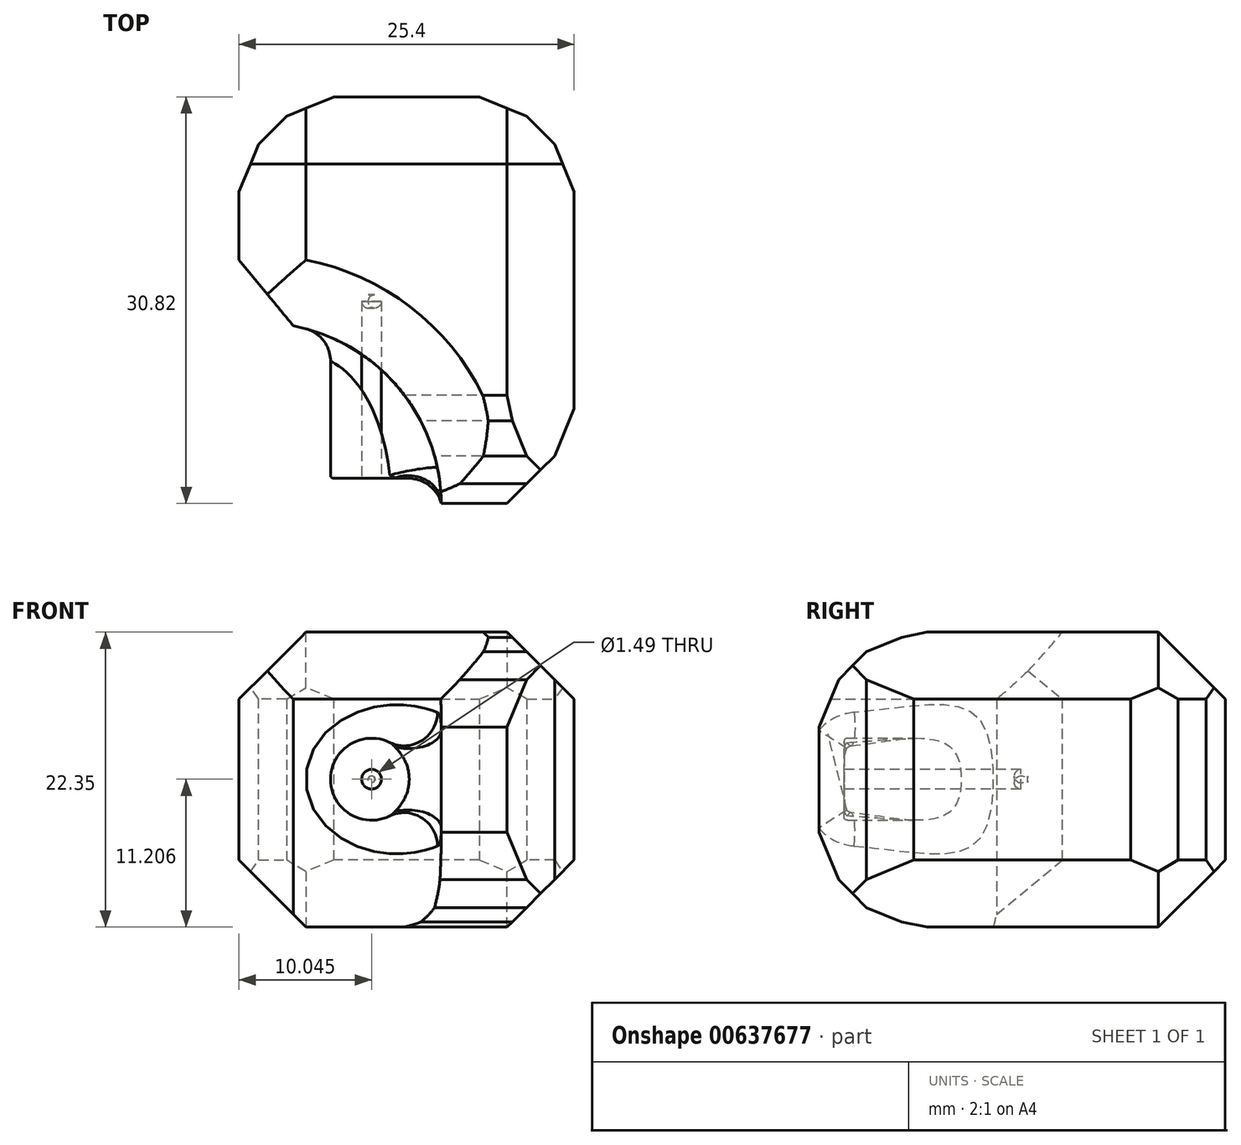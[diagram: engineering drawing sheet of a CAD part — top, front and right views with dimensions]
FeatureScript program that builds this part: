
annotation { "Feature Type Name" : "Feature", "Feature Type Description" : "" }
export const myFeature = defineFeature(function(context is Context, id is Id, definition is map)
    precondition{}
    {
        {
            var Q0;
            Q0=qCreatedBy(makeId("Top.planeOp"),FACE);
            var sketch = newSketch(context, id + "F0", { "sketchPlane" : qUnion([Q0])});
            skLineSegment(sketch, "E0.bottom", {"start": v(-10.5, 17.8) * mm, "end": v(14.9, 17.8) * mm});
            skLineSegment(sketch, "E0.top", {"start": v(-10.5, -13.03) * mm, "end": v(14.9, -13.03) * mm});
            skLineSegment(sketch, "E0.left", {"start": v(-10.5, 17.8) * mm, "end": v(-10.5, -13.03) * mm});
            skLineSegment(sketch, "E0.right", {"start": v(14.9, 17.8) * mm, "end": v(14.9, -13.03) * mm});
            skSolve(sketch);
        }
        {
            var Q0;
            Q0 = qSketchRegion(id + "F0", true);
            extrude(context, id + "F1", {"entities" : qUnion([Q0]), "depth" : 22.35 * mm, "offsetDistance" : 25.4 * mm});
        }
        {
            var Q0;
            Q0=makeQuery(id+"F1.opExtrude","SWEPT_EDGE",EDGE,{"disambiguationData":[OSD([sQuery(id+"F0.wireOp",EDGE,"E0.bottom"),sQuery(id+"F0.wireOp",EDGE,"E0.left")])]});
            var Q1;
            Q1=makeQuery(id+"F1.opExtrude","SWEPT_EDGE",EDGE,{"disambiguationData":[OSD([sQuery(id+"F0.wireOp",EDGE,"E0.bottom"),sQuery(id+"F0.wireOp",EDGE,"E0.right")])]});
            var Q2;
            Q2=makeQuery(id+"F1.opExtrude","SWEPT_EDGE",EDGE,{"disambiguationData":[OSD([sQuery(id+"F0.wireOp",EDGE,"E0.top"),sQuery(id+"F0.wireOp",EDGE,"E0.right")])]});
            var Q3;
            Q3=makeQuery(id+"F1.opExtrude","SWEPT_EDGE",EDGE,{"disambiguationData":[OSD([sQuery(id+"F0.wireOp",EDGE,"E0.top"),sQuery(id+"F0.wireOp",EDGE,"E0.left")])]});
            var Q4;
            Q4=makeQuery(id+"F1.opExtrude","CAP_EDGE",EDGE,{"disambiguationData":[OSD([sQuery(id+"F0.wireOp",EDGE,"E0.right")])],"isStart":false});
            var Q5;
            Q5=makeQuery(id+"F1.opExtrude","CAP_EDGE",EDGE,{"disambiguationData":[OSD([sQuery(id+"F0.wireOp",EDGE,"E0.right")])],"isStart":true});
            var Q6;
            Q6=makeQuery(id+"F1.opExtrude","CAP_EDGE",EDGE,{"disambiguationData":[OSD([sQuery(id+"F0.wireOp",EDGE,"E0.bottom")])],"isStart":false});
            var Q7;
            Q7=makeQuery(id+"F1.opExtrude","CAP_EDGE",EDGE,{"disambiguationData":[OSD([sQuery(id+"F0.wireOp",EDGE,"E0.bottom")])],"isStart":true});
            var Q8;
            Q8=makeQuery(id+"F1.opExtrude","CAP_EDGE",EDGE,{"disambiguationData":[OSD([sQuery(id+"F0.wireOp",EDGE,"E0.left")])],"isStart":true});
            var Q9;
            Q9=makeQuery(id+"F1.opExtrude","CAP_EDGE",EDGE,{"disambiguationData":[OSD([sQuery(id+"F0.wireOp",EDGE,"E0.left")])],"isStart":false});
            chamfer(context, id + "F2", {"entities" : qUnion([Q0, Q1, Q2, Q3, Q4, Q5, Q6, Q7, Q8, Q9]), "width" : 5.08 * mm, "tangentPropagation" : true});
        }
        {
            var Q0;
            Q0=qCreatedBy(makeId("Top.planeOp"),FACE);
            var sketch = newSketch(context, id + "F3", { "sketchPlane" : qUnion([Q0])});
            skCircle(sketch, "E1", {"center": v(-9.02, -13.17) * mm, "radius": 13.85 * mm});
            skSolve(sketch);
        }
        {
            var Q0;
            Q0=makeQuery(id+"F3.imprint","IMPRINT",FACE,{"disambiguationData":[TD([[makeQuery(id+"F3.imprint","IMPRINT",EDGE,{"derivedFrom":sQuery(id+"F3.wireOp",EDGE,"E1")}),1.0]])]});
            extrude(context, id + "F4", {"entities" : qUnion([Q0]), "operationType" : NewBodyOperationType.REMOVE, "depth" : 27.86 * mm, "offsetDistance" : 25.4 * mm});
        }
        {
            var Q0;
            Q0=qCreatedBy(makeId("Front.planeOp"),FACE);
            var sketch = newSketch(context, id + "F5", { "sketchPlane" : qUnion([Q0])});
            skCircle(sketch, "E2", {"center": v(-0.45, 11.2) * mm, "radius": 3.11 * mm});
            skSolve(sketch);
        }
        {
            var Q0;
            Q0 = qSketchRegion(id + "F5", true);
            var Q1;
            Q1 = qConstructionFilter(qBodyType(qCreatedBy(id + "F5" ,EDGE), BodyType.WIRE), ConstructionObject.NO);
            extrude(context, id + "F6", {"entities" : qUnion([Q0]), "operationType" : NewBodyOperationType.ADD, "surfaceEntities" : qUnion([Q1]), "depth" : 11.13 * mm, "offsetDistance" : 25.4 * mm});
        }
        {
            var Q0;
            Q0=makeQuery(id+"F6.opExtrude","CAP_EDGE",EDGE,{"disambiguationData":[OSD([sQuery(id+"F5.wireOp",EDGE,"E2")])],"isStart":false});
            fillet(context, id + "F7", {"entities" : qUnion([Q0]), "radius" : 0.25 * mm, "tangentPropagation" : true, "allowEdgeOverflow" : false});
        }
        {
            var Q0;
            Q0=makeQuery(id+"F6.boolean.opBoolean","INTERSECT",EDGE,{"derivedFrom":[makeQuery(id+"F4.boolean.opBoolean","COPY",FACE,{"derivedFrom":makeQuery(id+"F4.opExtrude","SWEPT_FACE",FACE,{"disambiguationData":[OSD([sQuery(id+"F3.wireOp",EDGE,"E1")])]})}),makeQuery(id+"F6.opExtrude","SWEPT_FACE",FACE,{"disambiguationData":[OSD([sQuery(id+"F5.wireOp",EDGE,"E2")])]})]});
            fillet(context, id + "F8", {"entities" : qUnion([Q0]), "radius" : 2.54 * mm, "tangentPropagation" : true, "allowEdgeOverflow" : false});
        }
        {
            var Q0;
            Q0=makeQuery(id+"F1.opExtrude","CAP_EDGE",EDGE,{"disambiguationData":[OSD([sQuery(id+"F0.wireOp",EDGE,"E0.top")])],"isStart":true});
            var Q1;
            Q1=makeQuery(id+"F1.opExtrude","CAP_EDGE",EDGE,{"disambiguationData":[OSD([sQuery(id+"F0.wireOp",EDGE,"E0.top")])],"isStart":false});
            chamfer(context, id + "F9", {"entities" : qUnion([Q0, Q1]), "width" : 5.08 * mm, "tangentPropagation" : true});
        }
        {
            var Q0;
            {var subQ0=sQuery(id+"F0.wireOp",EDGE,"E0.top");Q0=makeQuery(id+"F9.opChamfer","BLEND_EDGE",EDGE,{"blendedFrom":[makeQuery(id+"F1.opExtrude","CAP_EDGE",EDGE,{"disambiguationData":[OSD([subQ0])],"isStart":true}),makeQuery(id+"F1.opExtrude","CAP_FACE",FACE,{"disambiguationData":[OSD([sQuery(id+"F0.wireOp",EDGE,"E0.bottom"),subQ0,sQuery(id+"F0.wireOp",EDGE,"E0.left"),sQuery(id+"F0.wireOp",EDGE,"E0.right")])],"isStart":true})],"blendedInto":[makeQuery(id+"F1.opExtrude","CAP_FACE",FACE,{"disambiguationData":[OSD([sQuery(id+"F0.wireOp",EDGE,"E0.bottom"),subQ0,sQuery(id+"F0.wireOp",EDGE,"E0.left"),sQuery(id+"F0.wireOp",EDGE,"E0.right")])],"isStart":true})]});}
            var Q1;
            {var subQ0=sQuery(id+"F0.wireOp",EDGE,"E0.top");Q1=makeQuery(id+"F9.opChamfer","BLEND_EDGE",EDGE,{"blendedFrom":[makeQuery(id+"F1.opExtrude","CAP_EDGE",EDGE,{"disambiguationData":[OSD([subQ0])],"isStart":false}),makeQuery(id+"F1.opExtrude","CAP_FACE",FACE,{"disambiguationData":[OSD([sQuery(id+"F0.wireOp",EDGE,"E0.bottom"),subQ0,sQuery(id+"F0.wireOp",EDGE,"E0.left"),sQuery(id+"F0.wireOp",EDGE,"E0.right")])],"isStart":false})],"blendedInto":[makeQuery(id+"F1.opExtrude","CAP_FACE",FACE,{"disambiguationData":[OSD([sQuery(id+"F0.wireOp",EDGE,"E0.bottom"),subQ0,sQuery(id+"F0.wireOp",EDGE,"E0.left"),sQuery(id+"F0.wireOp",EDGE,"E0.right")])],"isStart":false})]});}
            chamfer(context, id + "F10", {"entities" : qUnion([Q0, Q1]), "width" : 5.08 * mm, "tangentPropagation" : true});
        }
        {
            var Q0;
            Q0=makeQuery(id+"F6.opExtrude","CAP_FACE",FACE,{"disambiguationData":[OSD([sQuery(id+"F5.wireOp",EDGE,"E2")])],"isStart":false});
            var sketch = newSketch(context, id + "F11", { "sketchPlane" : qUnion([Q0])});
            skCircle(sketch, "E3", {"center": v(-0.45, 11.2) * mm, "radius": 0.75 * mm});
            skSolve(sketch);
        }
        {
            var Q0;
            Q0=makeQuery(id+"F11.imprint","IMPRINT",FACE,{"disambiguationData":[TD([[makeQuery(id+"F11.imprint","IMPRINT",EDGE,{"derivedFrom":sQuery(id+"F11.wireOp",EDGE,"E3")}),1.0]])]});
            extrude(context, id + "F12", {"entities" : qUnion([Q0]), "operationType" : NewBodyOperationType.REMOVE, "oppositeDirection" : true, "depth" : 13.92 * mm, "offsetDistance" : 25.4 * mm});
        }
        {
            var Q0;
            Q0=makeQuery(id+"F12.boolean.opBoolean","COPY",EDGE,{"derivedFrom":makeQuery(id+"F12.opExtrude","CAP_EDGE",EDGE,{"disambiguationData":[OSD([sQuery(id+"F11.wireOp",EDGE,"E3")])],"isStart":false})});
            fillet(context, id + "F13", {"entities" : qUnion([Q0]), "radius" : 0.5 * mm, "tangentPropagation" : true, "allowEdgeOverflow" : false});
        }
        {
            var Q0;
            Q0=makeQuery(id+"F4.boolean.opBoolean","COPY",EDGE,{"derivedFrom":makeQuery(id+"F4.opExtrude","CAP_EDGE",EDGE,{"disambiguationData":[OSD([sQuery(id+"F3.wireOp",EDGE,"E1")])],"isStart":true})});
            var Q1;
            Q1=makeQuery(id+"F4.boolean.opBoolean","INTERSECT",EDGE,{"derivedFrom":[makeQuery(id+"F1.opExtrude","CAP_FACE",FACE,{"disambiguationData":[OSD([sQuery(id+"F0.wireOp",EDGE,"E0.bottom"),sQuery(id+"F0.wireOp",EDGE,"E0.top"),sQuery(id+"F0.wireOp",EDGE,"E0.left"),sQuery(id+"F0.wireOp",EDGE,"E0.right")])],"isStart":false}),makeQuery(id+"F4.opExtrude","SWEPT_FACE",FACE,{"disambiguationData":[OSD([sQuery(id+"F3.wireOp",EDGE,"E1")])]})]});
            var Q2;
            Q2=makeQuery(id+"F4.boolean.opBoolean","INTERSECT",EDGE,{"derivedFrom":[makeQuery(id+"F1.opExtrude","SWEPT_FACE",FACE,{"disambiguationData":[OSD([sQuery(id+"F0.wireOp",EDGE,"E0.left")])]}),makeQuery(id+"F4.opExtrude","SWEPT_FACE",FACE,{"disambiguationData":[OSD([sQuery(id+"F3.wireOp",EDGE,"E1")])]})]});
            var Q3;
            {var subQ0=sQuery(id+"F0.wireOp",EDGE,"E0.bottom");Q3=makeQuery(id+"F2.opChamfer","BLEND_EDGE",EDGE,{"blendedFrom":[makeQuery(id+"F1.opExtrude","SWEPT_EDGE",EDGE,{"disambiguationData":[OSD([subQ0,sQuery(id+"F0.wireOp",EDGE,"E0.right")])]}),makeQuery(id+"F1.opExtrude","SWEPT_FACE",FACE,{"disambiguationData":[OSD([subQ0])]})],"blendedInto":[makeQuery(id+"F1.opExtrude","SWEPT_FACE",FACE,{"disambiguationData":[OSD([subQ0])]})]});}
            var Q4;
            {var subQ0=sQuery(id+"F0.wireOp",EDGE,"E0.right");Q4=makeQuery(id+"F2.opChamfer","BLEND_EDGE",EDGE,{"blendedFrom":[makeQuery(id+"F1.opExtrude","SWEPT_EDGE",EDGE,{"disambiguationData":[OSD([sQuery(id+"F0.wireOp",EDGE,"E0.bottom"),subQ0])]}),makeQuery(id+"F1.opExtrude","SWEPT_FACE",FACE,{"disambiguationData":[OSD([subQ0])]})],"blendedInto":[makeQuery(id+"F1.opExtrude","SWEPT_FACE",FACE,{"disambiguationData":[OSD([subQ0])]})]});}
            var Q5;
            {var subQ0=sQuery(id+"F0.wireOp",EDGE,"E0.right");Q5=makeQuery(id+"F2.opChamfer","BLEND_EDGE",EDGE,{"blendedFrom":[makeQuery(id+"F1.opExtrude","SWEPT_EDGE",EDGE,{"disambiguationData":[OSD([sQuery(id+"F0.wireOp",EDGE,"E0.top"),subQ0])]}),makeQuery(id+"F1.opExtrude","SWEPT_FACE",FACE,{"disambiguationData":[OSD([subQ0])]})],"blendedInto":[makeQuery(id+"F1.opExtrude","SWEPT_FACE",FACE,{"disambiguationData":[OSD([subQ0])]})]});}
            var Q6;
            {var subQ0=sQuery(id+"F0.wireOp",EDGE,"E0.top");Q6=makeQuery(id+"F9.opChamfer","BLEND_EDGE",EDGE,{"blendedFrom":[makeQuery(id+"F1.opExtrude","CAP_EDGE",EDGE,{"disambiguationData":[OSD([subQ0])],"isStart":false}),makeQuery(id+"F1.opExtrude","SWEPT_FACE",FACE,{"disambiguationData":[OSD([subQ0])]})],"blendedInto":[makeQuery(id+"F1.opExtrude","SWEPT_FACE",FACE,{"disambiguationData":[OSD([subQ0])]})]});}
            var Q7;
            {var subQ0=sQuery(id+"F0.wireOp",EDGE,"E0.top");Q7=makeQuery(id+"F9.opChamfer","BLEND_EDGE",EDGE,{"blendedFrom":[makeQuery(id+"F1.opExtrude","CAP_EDGE",EDGE,{"disambiguationData":[OSD([subQ0])],"isStart":true}),makeQuery(id+"F1.opExtrude","SWEPT_FACE",FACE,{"disambiguationData":[OSD([subQ0])]})],"blendedInto":[makeQuery(id+"F1.opExtrude","SWEPT_FACE",FACE,{"disambiguationData":[OSD([subQ0])]})]});}
            var Q8;
            {var subQ0=sQuery(id+"F0.wireOp",EDGE,"E0.left");Q8=makeQuery(id+"F2.opChamfer","BLEND_EDGE",EDGE,{"blendedFrom":[makeQuery(id+"F1.opExtrude","SWEPT_EDGE",EDGE,{"disambiguationData":[OSD([sQuery(id+"F0.wireOp",EDGE,"E0.bottom"),subQ0])]}),makeQuery(id+"F1.opExtrude","SWEPT_FACE",FACE,{"disambiguationData":[OSD([subQ0])]})],"blendedInto":[makeQuery(id+"F1.opExtrude","SWEPT_FACE",FACE,{"disambiguationData":[OSD([subQ0])]})]});}
            var Q9;
            {var subQ0=sQuery(id+"F0.wireOp",EDGE,"E0.bottom");Q9=makeQuery(id+"F2.opChamfer","BLEND_EDGE",EDGE,{"blendedFrom":[makeQuery(id+"F1.opExtrude","SWEPT_EDGE",EDGE,{"disambiguationData":[OSD([subQ0,sQuery(id+"F0.wireOp",EDGE,"E0.left")])]}),makeQuery(id+"F1.opExtrude","SWEPT_FACE",FACE,{"disambiguationData":[OSD([subQ0])]})],"blendedInto":[makeQuery(id+"F1.opExtrude","SWEPT_FACE",FACE,{"disambiguationData":[OSD([subQ0])]})]});}
            chamfer(context, id + "F14", {"entities" : qUnion([Q0, Q1, Q2, Q3, Q4, Q5, Q6, Q7, Q8, Q9]), "width" : 5.08 * mm, "tangentPropagation" : true});
        }
        {
            var Q0;
            {var subQ0=sQuery(id+"F0.wireOp",EDGE,"E0.top");var subQ1=makeQuery(id+"F1.opExtrude","CAP_FACE",FACE,{"disambiguationData":[OSD([sQuery(id+"F0.wireOp",EDGE,"E0.bottom"),subQ0,sQuery(id+"F0.wireOp",EDGE,"E0.left"),sQuery(id+"F0.wireOp",EDGE,"E0.right")])],"isStart":false});Q0=makeQuery(id+"F10.opChamfer","BLEND_EDGE",EDGE,{"blendedFrom":[makeQuery(id+"F9.opChamfer","BLEND_EDGE",EDGE,{"blendedFrom":[makeQuery(id+"F1.opExtrude","CAP_EDGE",EDGE,{"disambiguationData":[OSD([subQ0])],"isStart":false}),subQ1],"blendedInto":[subQ1]}),subQ1],"blendedInto":[subQ1]});}
            var Q1;
            {var subQ0=sQuery(id+"F0.wireOp",EDGE,"E0.top");var subQ1=makeQuery(id+"F1.opExtrude","CAP_FACE",FACE,{"disambiguationData":[OSD([sQuery(id+"F0.wireOp",EDGE,"E0.bottom"),subQ0,sQuery(id+"F0.wireOp",EDGE,"E0.left"),sQuery(id+"F0.wireOp",EDGE,"E0.right")])],"isStart":true});Q1=makeQuery(id+"F10.opChamfer","BLEND_EDGE",EDGE,{"blendedFrom":[makeQuery(id+"F9.opChamfer","BLEND_EDGE",EDGE,{"blendedFrom":[makeQuery(id+"F1.opExtrude","CAP_EDGE",EDGE,{"disambiguationData":[OSD([subQ0])],"isStart":true}),subQ1],"blendedInto":[subQ1]}),subQ1],"blendedInto":[subQ1]});}
            chamfer(context, id + "F15", {"entities" : qUnion([Q0, Q1]), "width" : 5.08 * mm, "tangentPropagation" : true});
        }
    });
